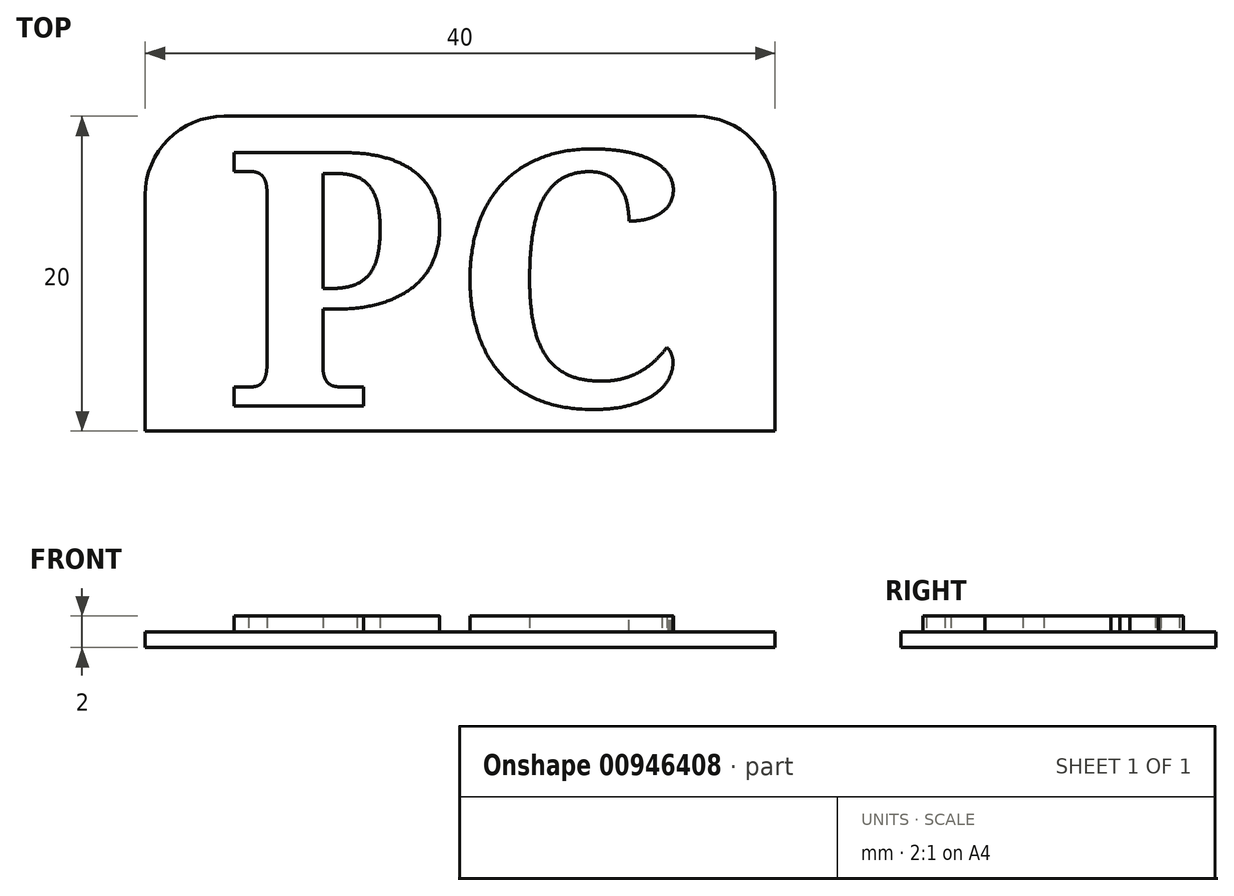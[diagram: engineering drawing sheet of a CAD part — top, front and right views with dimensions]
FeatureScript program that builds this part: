
annotation { "Feature Type Name" : "Feature", "Feature Type Description" : "" }
export const myFeature = defineFeature(function(context is Context, id is Id, definition is map)
    precondition{}
    {
        {
            var Q0;
            Q0=qCreatedBy(makeId("Top.planeOp"),FACE);
            var sketch = newSketch(context, id + "F0", { "sketchPlane" : qUnion([Q0])});
            skLineSegment(sketch, "E0.bottom", {"start": v(-20, 10) * mm, "end": v(20, 10) * mm});
            skLineSegment(sketch, "E0.top", {"start": v(-20, -10) * mm, "end": v(20, -10) * mm});
            skLineSegment(sketch, "E0.left", {"start": v(-20, 10) * mm, "end": v(-20, -10) * mm});
            skLineSegment(sketch, "E0.right", {"start": v(20, 10) * mm, "end": v(20, -10) * mm});
            skPoint(sketch, "E0.middle", {"position": v(0, 0) * mm});
            skSolve(sketch);
        }
        {
            var Q0;
            Q0=makeQuery(id+"F0.imprint","IMPRINT",FACE,{"disambiguationData":[TD([[makeQuery(id+"F0.imprint","IMPRINT",EDGE,{"derivedFrom":sQuery(id+"F0.wireOp",EDGE,"E0.bottom")}),-1.0]])]});
            extrude(context, id + "F1", {"entities" : qUnion([Q0]), "depth" : 1 * mm, "offsetDistance" : 25 * mm});
        }
        {
            var Q0;
            Q0=makeQuery(id+"F1.opExtrude","CAP_FACE",FACE,{"disambiguationData":[OSD([sQuery(id+"F0.wireOp",EDGE,"E0.bottom"),sQuery(id+"F0.wireOp",EDGE,"E0.top"),sQuery(id+"F0.wireOp",EDGE,"E0.left"),sQuery(id+"F0.wireOp",EDGE,"E0.right")])],"isStart":false});
            var sketch = newSketch(context, id + "F2", { "sketchPlane" : qUnion([Q0])});
            skText(sketch, "E1", { "text": "PC", "fontName": "NotoSerif-Bold.ttf"});
            const initialGuessF2  = {"E1": [-0.015, -0.0084, 1, 0, 0.01623]};
            skSetInitialGuess(sketch, initialGuessF2);
            skSolve(sketch);
        }
        {
            var Q0;
            Q0=qSketchRegion(id+"F2",true);
            extrude(context, id + "F3", {"entities" : qUnion([Q0]), "operationType" : NewBodyOperationType.ADD, "depth" : 1 * mm, "offsetDistance" : 25 * mm});
        }
        {
            var Q0;
            Q0=makeQuery(id+"F1.opExtrude","SWEPT_EDGE",EDGE,{"disambiguationData":[OSD([sQuery(id+"F0.wireOp",EDGE,"E0.bottom"),sQuery(id+"F0.wireOp",EDGE,"E0.left")])]});
            var Q1;
            Q1=makeQuery(id+"F1.opExtrude","SWEPT_EDGE",EDGE,{"disambiguationData":[OSD([sQuery(id+"F0.wireOp",EDGE,"E0.bottom"),sQuery(id+"F0.wireOp",EDGE,"E0.right")])]});
            fillet(context, id + "F4", {"entities" : qUnion([Q0, Q1]), "radius" : 5 * mm, "tangentPropagation" : true, "allowEdgeOverflow" : false});
        }
    });
